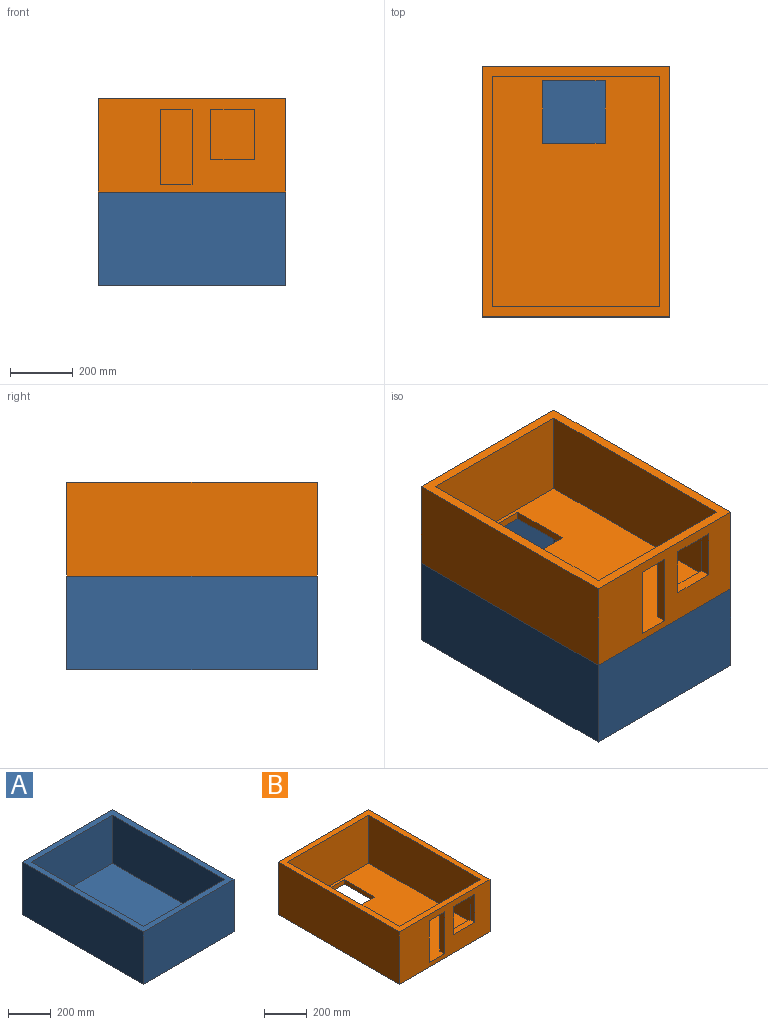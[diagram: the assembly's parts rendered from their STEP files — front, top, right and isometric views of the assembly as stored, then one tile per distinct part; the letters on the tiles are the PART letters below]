
ASSEMBLY  parts=2 mates=1
PART A: 11 faces, bbox 600x800x300 mm
  f0: plane 536x275mm, normal (0,1,0), area 147400mm2, adj f1,f7,f8,f10
  f1: plane 736x275mm, normal (1,0,0), area 202400mm2, adj f0,f2,f8,f10
  f2: plane 536x275mm, normal (0,-1,0), area 147400mm2, adj f1,f7,f8,f10
  f3: plane 800x300mm, normal (-1,0,0), area 240000mm2, adj f4,f6,f8,f9
  f4: plane 600x300mm, normal (0,-1,0), area 180000mm2, adj f3,f5,f8,f9
  f5: plane 800x300mm, normal (1,0,0), area 240000mm2, adj f4,f6,f8,f9
  f6: plane 600x300mm, normal (0,1,0), area 180000mm2, adj f3,f5,f8,f9
  f7: plane 736x275mm, normal (-1,0,0), area 202400mm2, adj f0,f2,f8,f10
  f8: plane 800x600mm, normal (0,0,1), area 85504mm2, adj f0,f1,f2,f3,f4,f5,f6,f7
  f9: plane 800x600mm, normal (0,0,-1), area 480000mm2, adj f3,f4,f5,f6
  f10: plane 736x536mm, normal (0,0,1), area 394496mm2, adj f0,f1,f2,f7
PART B: 22 faces, bbox 600x800x300 mm
  f0: plane 536x275mm, normal (0,1,0), area 101000mm2, adj f2,f7,f8,f10,f11,f12,f13,f14
  f1: plane 600x300mm, normal (0,-1,0), area 133600mm2, adj f4,f5,f8,f9,f10,f11,f12,f13
  f2: plane 736x275mm, normal (1,0,0), area 202400mm2, adj f0,f3,f8,f10
  f3: plane 536x275mm, normal (0,-1,0), area 147400mm2, adj f2,f7,f8,f10
  f4: plane 800x300mm, normal (-1,0,0), area 240000mm2, adj f1,f6,f8,f9
  f5: plane 800x300mm, normal (1,0,0), area 240000mm2, adj f1,f6,f8,f9
  f6: plane 600x300mm, normal (0,1,0), area 180000mm2, adj f4,f5,f8,f9
  f7: plane 736x275mm, normal (-1,0,0), area 202400mm2, adj f0,f3,f8,f10
  f8: plane 800x600mm, normal (0,0,1), area 85504mm2, adj f0,f1,f2,f3,f4,f5,f6,f7
  f9: plane 800x600mm, normal (0,0,-1), area 440000mm2, adj f1,f4,f5,f6,f18,f19,f20,f21
  f10: plane 768x536mm, normal (0,0,1), area 357696mm2, adj f0,f1,f2,f3,f7,f16,f17,f18
  f11: plane 140x32mm, normal (0,0,-1), area 4480mm2, adj f0,f1,f12,f14
  f12: plane 160x32mm, normal (1,0,0), area 5120mm2, adj f0,f1,f11,f13
  f13: plane 140x32mm, normal (0,0,1), area 4480mm2, adj f0,f1,f12,f14
  f14: plane 160x32mm, normal (-1,0,0), area 5120mm2, adj f0,f1,f11,f13
  f15: plane 100x32mm, normal (0,0,-1), area 3200mm2, adj f0,f1,f16,f17
  f16: plane 240x32mm, normal (1,0,0), area 7680mm2, adj f0,f1,f10,f15
  f17: plane 240x32mm, normal (-1,0,0), area 7680mm2, adj f0,f1,f10,f15
  f18: plane 200x25mm, normal (1,0,0), area 5000mm2, adj f9,f10,f19,f21
  f19: plane 200x25mm, normal (0,1,0), area 5000mm2, adj f9,f10,f18,f20
  f20: plane 200x25mm, normal (-1,0,0), area 5000mm2, adj f9,f10,f19,f21
  f21: plane 200x25mm, normal (0,-1,0), area 5000mm2, adj f9,f10,f18,f20
PLACE A t=(-24.21,-79.08,-398.19)mm
PLACE B t=(-24.21,-79.08,-98.19)mm
MATE fastened B.f4 <-> A.f3  axis (-1,0,0) through (-426.16,-80.75,51.81)mm
